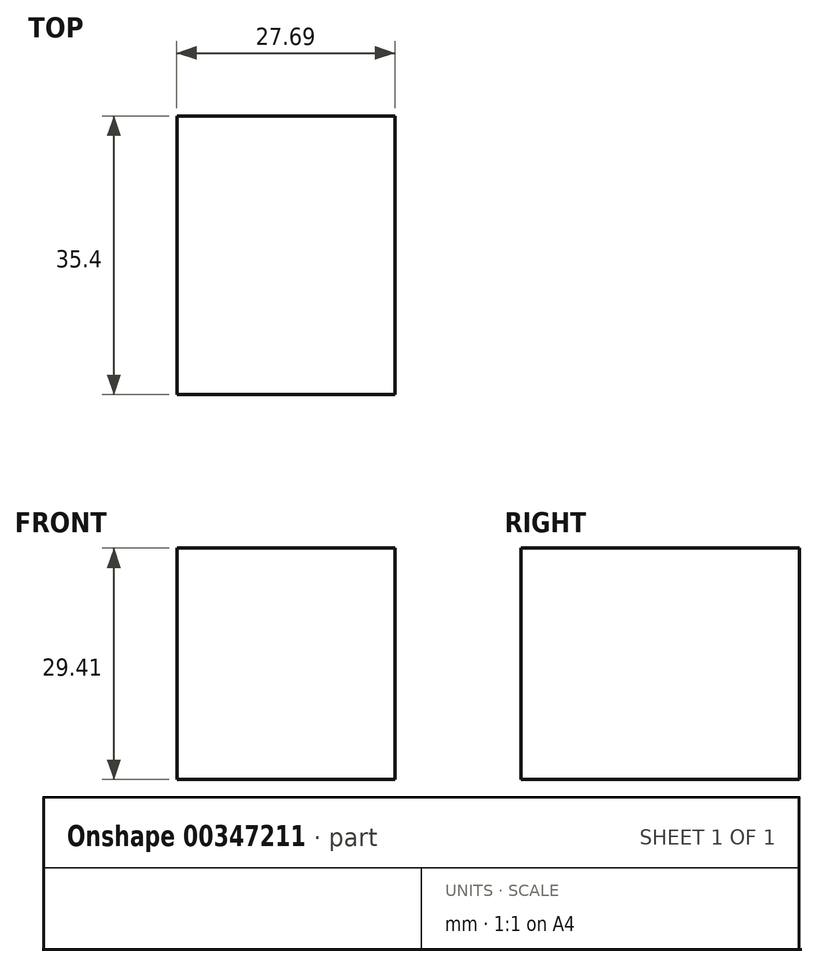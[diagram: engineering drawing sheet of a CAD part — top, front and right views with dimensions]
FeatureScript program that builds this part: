
annotation { "Feature Type Name" : "Feature", "Feature Type Description" : "" }
export const myFeature = defineFeature(function(context is Context, id is Id, definition is map)
    precondition{}
    {
        {
            var Q0;
            Q0=qCreatedBy(makeId("Front.planeOp"),FACE);
            var sketch = newSketch(context, id + "F0", { "sketchPlane" : qUnion([Q0])});
            skLineSegment(sketch, "E0.bottom", {"start": v(-12.62, 15.17) * mm, "end": v(15.07, 15.17) * mm});
            skLineSegment(sketch, "E0.top", {"start": v(-12.62, -14.24) * mm, "end": v(15.07, -14.24) * mm});
            skLineSegment(sketch, "E0.left", {"start": v(-12.62, 15.17) * mm, "end": v(-12.62, -14.24) * mm});
            skLineSegment(sketch, "E0.right", {"start": v(15.07, 15.17) * mm, "end": v(15.07, -14.24) * mm});
            skSolve(sketch);
        }
        {
            var Q0;
            Q0 = qSketchRegion(id + "F0", true);
            extrude(context, id + "F1", {"entities" : qUnion([Q0]), "depth" : 10 * mm, "hasSecondDirection" : true, "secondDirectionOppositeDirection" : true, "secondDirectionDepth" : 25.4 * mm});
        }
    });
